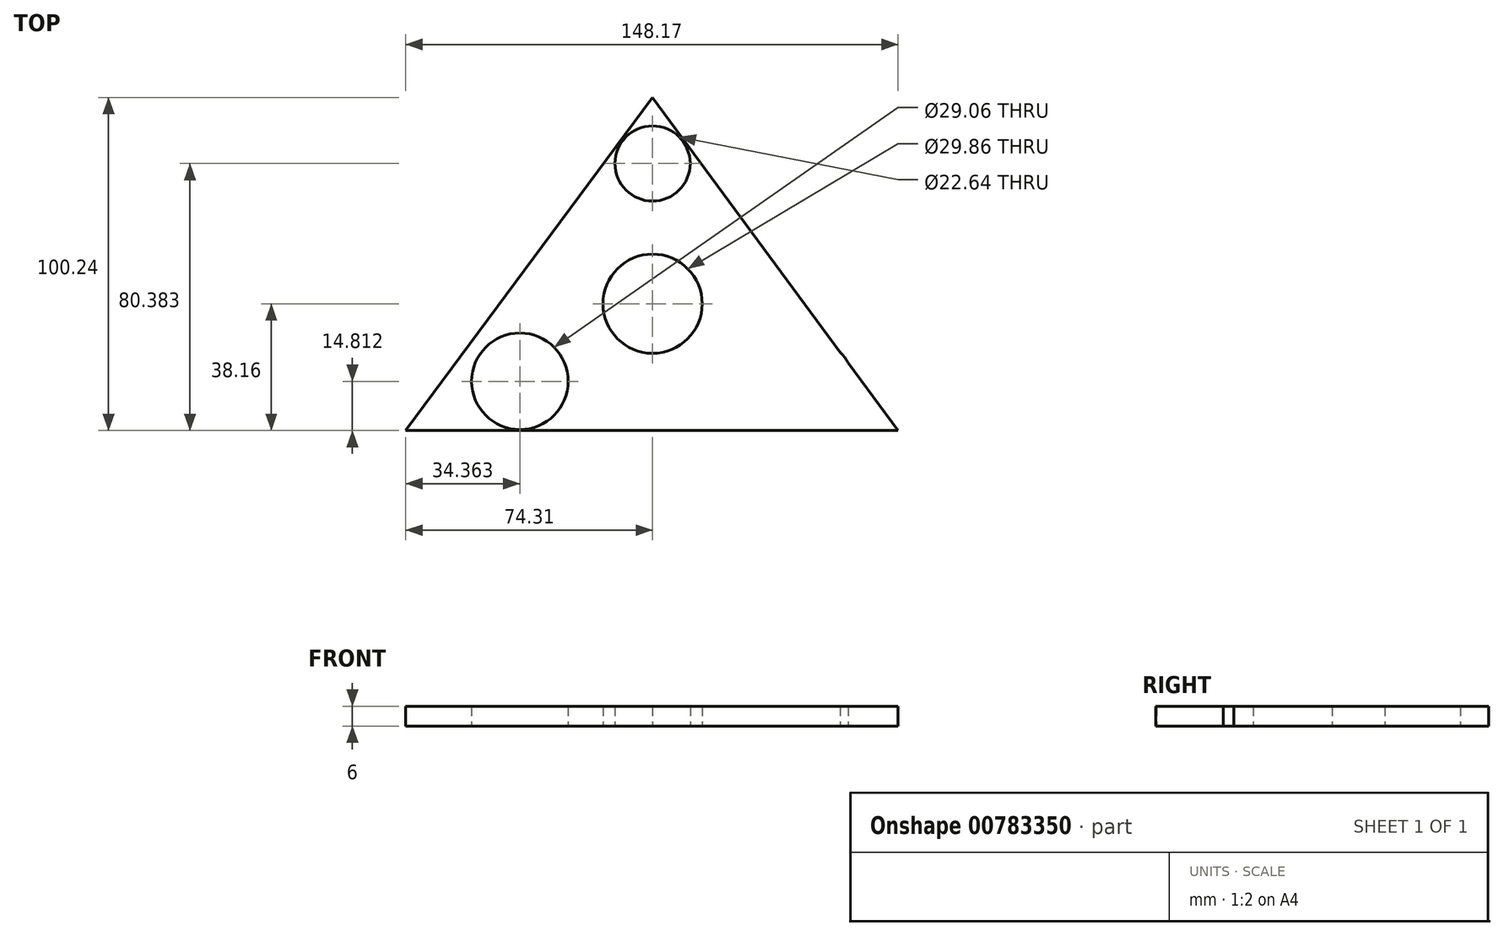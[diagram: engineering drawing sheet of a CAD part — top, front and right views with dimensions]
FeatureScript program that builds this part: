
annotation { "Feature Type Name" : "Feature", "Feature Type Description" : "" }
export const myFeature = defineFeature(function(context is Context, id is Id, definition is map)
    precondition{}
    {
        {
            var Q0;
            Q0=qCreatedBy(makeId("Top.planeOp"),FACE);
            var sketch = newSketch(context, id + "F0", { "sketchPlane" : qUnion([Q0])});
            skLineSegment(sketch, "E0", {"start": v(-49.7, 0) * mm, "end": v(39, 0) * mm});
            skLineSegment(sketch, "E1", {"start": v(0, 62.08) * mm, "end": v(-74.3, -38.16) * mm});
            skLineSegment(sketch, "E2", {"start": v(-74.3, -38.16) * mm, "end": v(73.86, -38.16) * mm});
            skLineSegment(sketch, "E3", {"start": v(73.86, -38.16) * mm, "end": v(0, 62.08) * mm});
            skCircle(sketch, "E4", {"center": v(0, 0) * mm, "radius": 14.93 * mm});
            skCircle(sketch, "E5", {"center": v(0, 42.22) * mm, "radius": 11.32 * mm});
            skCircle(sketch, "E6", {"center": v(-39.95, -23.35) * mm, "radius": 14.53 * mm});
            skCircle(sketch, "E7", {"center": v(46.75, -24.3) * mm, "radius": 13.74 * mm});
            skSolve(sketch);
        }
        {
            var Q0;
            Q0=qSketchRegion(id+"F0",true);
            extrude(context, id + "F1", {"entities" : qUnion([Q0]), "depth" : 6 * mm, "offsetDistance" : 25 * mm});
        }
        {
            var Q0;
            Q0=sQuery(id+"F0.wireOp",EDGE,"E7");
            extrude(context, id + "F2", {"bodyType" : ToolBodyType.SURFACE, "surfaceEntities" : qUnion([Q0]), "depth" : 6 * mm, "offsetDistance" : 25 * mm});
        }
    });
